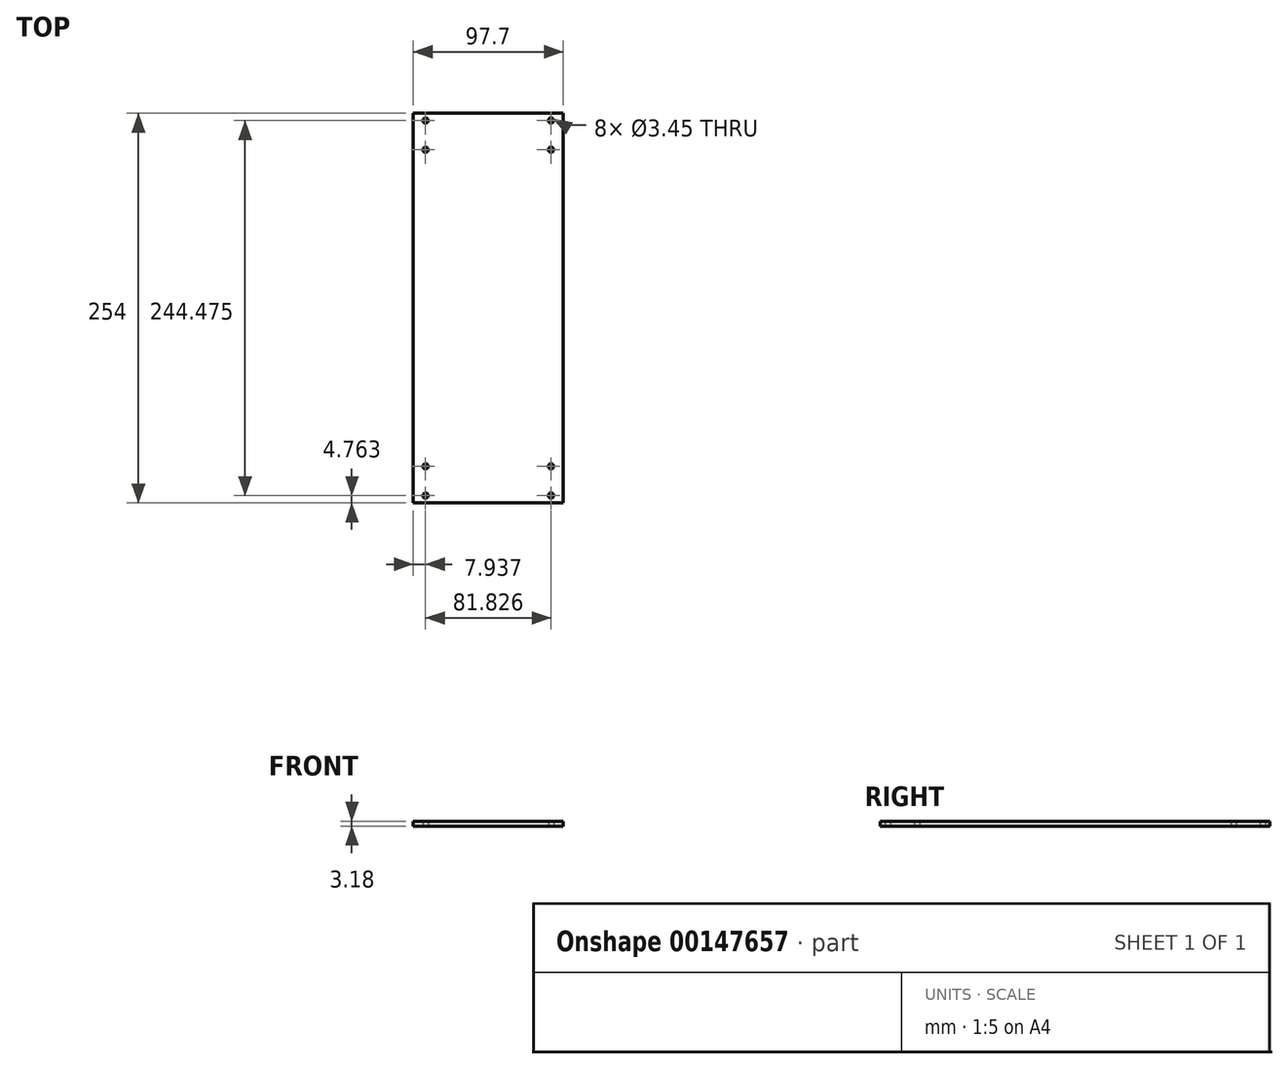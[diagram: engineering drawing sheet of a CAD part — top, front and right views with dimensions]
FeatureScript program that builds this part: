
annotation { "Feature Type Name" : "Feature", "Feature Type Description" : "" }
export const myFeature = defineFeature(function(context is Context, id is Id, definition is map)
    precondition{}
    {
        {
            var Q0;
            Q0=qCreatedBy(makeId("Top.planeOp"),FACE);
            var sketch = newSketch(context, id + "F0", { "sketchPlane" : qUnion([Q0])});
            skLineSegment(sketch, "E0.bottom", {"start": v(48.85, -127) * mm, "end": v(-48.85, -127) * mm});
            skLineSegment(sketch, "E0.top", {"start": v(48.85, 127) * mm, "end": v(-48.85, 127) * mm});
            skLineSegment(sketch, "E0.left", {"start": v(48.85, -127) * mm, "end": v(48.85, 127) * mm});
            skLineSegment(sketch, "E0.right", {"start": v(-48.85, -127) * mm, "end": v(-48.85, 127) * mm});
            skPoint(sketch, "E0.middle", {"position": v(0, 0) * mm});
            skLineSegment(sketch, "E1", {"start": v(40.91, 103.19) * mm, "end": v(48.85, 103.19) * mm, "construction": true});
            skLineSegment(sketch, "E2.bottom", {"start": v(40.91, 103.19) * mm, "end": v(-40.91, 103.19) * mm, "construction": true});
            skLineSegment(sketch, "E2.top", {"start": v(40.91, -103.19) * mm, "end": v(-40.91, -103.19) * mm, "construction": true});
            skLineSegment(sketch, "E2.left", {"start": v(40.91, 103.19) * mm, "end": v(40.91, -103.19) * mm, "construction": true});
            skLineSegment(sketch, "E2.right", {"start": v(-40.91, 103.19) * mm, "end": v(-40.91, -103.19) * mm, "construction": true});
            skCircle(sketch, "E3", {"center": v(40.91, 103.19) * mm, "radius": 1.73 * mm});
            skCircle(sketch, "E4", {"center": v(-40.91, -103.19) * mm, "radius": 1.73 * mm});
            skLineSegment(sketch, "E5", {"start": v(0, 103.19) * mm, "end": v(0, 127) * mm, "construction": true});
            skLineSegment(sketch, "E6", {"start": v(40.91, 103.19) * mm, "end": v(40.91, 122.24) * mm, "construction": true});
            skCircle(sketch, "E7", {"center": v(-40.91, 103.19) * mm, "radius": 1.73 * mm});
            skCircle(sketch, "E8", {"center": v(40.91, -103.19) * mm, "radius": 1.73 * mm});
            skLineSegment(sketch, "E9", {"start": v(40.91, 122.24) * mm, "end": v(40.91, 127) * mm, "construction": true});
            skCircle(sketch, "E10", {"center": v(40.91, 122.24) * mm, "radius": 1.73 * mm});
            skLineSegment(sketch, "E11", {"start": v(-40.91, 103.19) * mm, "end": v(-40.91, 122.24) * mm, "construction": true});
            skLineSegment(sketch, "E12", {"start": v(-40.91, 122.24) * mm, "end": v(-40.91, 127) * mm, "construction": true});
            skLineSegment(sketch, "E13", {"start": v(-40.91, -103.19) * mm, "end": v(-40.91, -122.24) * mm, "construction": true});
            skLineSegment(sketch, "E14", {"start": v(-40.91, -122.24) * mm, "end": v(-40.91, -127) * mm, "construction": true});
            skLineSegment(sketch, "E15", {"start": v(40.91, -103.19) * mm, "end": v(40.91, -122.24) * mm, "construction": true});
            skLineSegment(sketch, "E16", {"start": v(40.91, -122.24) * mm, "end": v(40.91, -127) * mm, "construction": true});
            skCircle(sketch, "E17", {"center": v(-40.91, 122.24) * mm, "radius": 1.73 * mm});
            skCircle(sketch, "E18", {"center": v(-40.91, -122.24) * mm, "radius": 1.73 * mm});
            skCircle(sketch, "E19", {"center": v(40.91, -122.24) * mm, "radius": 1.73 * mm});
            skSolve(sketch);
        }
        {
            var Q0;
            Q0=makeQuery(id+"F0.imprint","IMPRINT",FACE,{"disambiguationData":[TD([[makeQuery(id+"F0.imprint","IMPRINT",EDGE,{"derivedFrom":sQuery(id+"F0.wireOp",EDGE,"E0.bottom")}),-1.0]])]});
            extrude(context, id + "F1", {"entities" : qUnion([Q0]), "depth" : 3.17 * mm});
        }
    });
